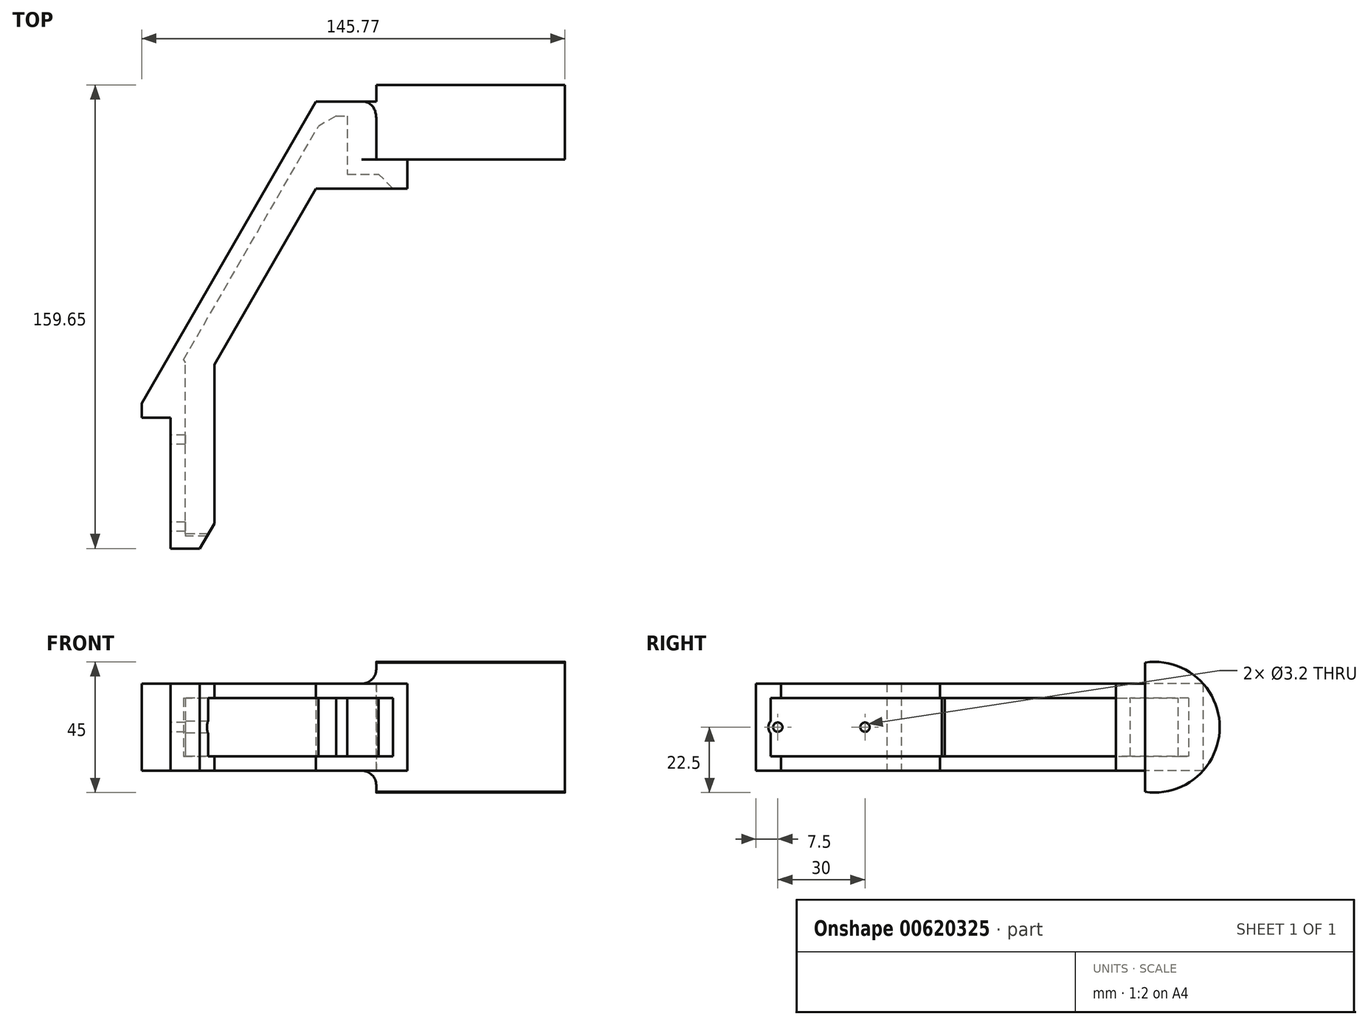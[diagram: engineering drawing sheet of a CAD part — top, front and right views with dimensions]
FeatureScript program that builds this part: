
annotation { "Feature Type Name" : "Feature", "Feature Type Description" : "" }
export const myFeature = defineFeature(function(context is Context, id is Id, definition is map)
    precondition{}
    {
        {
            var Q0;
            Q0=qCreatedBy(makeId("Top.planeOp"),FACE);
            var sketch = newSketch(context, id + "F0", { "sketchPlane" : qUnion([Q0])});
            skLineSegment(sketch, "E0", {"start": v(-10, 0) * mm, "end": v(-10, 5) * mm});
            skLineSegment(sketch, "E1", {"start": v(-10, 5) * mm, "end": v(50, 108.92) * mm});
            skLineSegment(sketch, "E2", {"start": v(81.55, 78.92) * mm, "end": v(10, -45) * mm});
            skLineSegment(sketch, "E3", {"start": v(10, -45) * mm, "end": v(0, -45) * mm});
            skLineSegment(sketch, "E4", {"start": v(50, 108.92) * mm, "end": v(65.77, 108.92) * mm});
            skLineSegment(sketch, "E5", {"start": v(81.55, 88.92) * mm, "end": v(81.55, 78.92) * mm});
            skLineSegment(sketch, "E6", {"start": v(0, -45) * mm, "end": v(0, 0) * mm});
            skLineSegment(sketch, "E7", {"start": v(0, 0) * mm, "end": v(-10, 0) * mm});
            skPoint(sketch, "E8.orphan", {"position": v(-10, -45) * mm});
            skLineSegment(sketch, "E9", {"start": v(65.77, 108.92) * mm, "end": v(65.77, 88.92) * mm});
            skLineSegment(sketch, "E10", {"start": v(65.77, 88.92) * mm, "end": v(81.55, 88.92) * mm});
            skPoint(sketch, "E11.orphan", {"position": v(81.55, 108.92) * mm});
            skSolve(sketch);
        }
        {
            var Q0;
            Q0=makeQuery(id+"F0.imprint","IMPRINT",FACE,{"disambiguationData":[TD([[makeQuery(id+"F0.imprint","IMPRINT",EDGE,{"derivedFrom":sQuery(id+"F0.wireOp",EDGE,"E0")}),-1.0]])]});
            extrude(context, id + "F1", {"entities" : qUnion([Q0]), "depth" : 30 * mm, "offsetDistance" : 25 * mm});
        }
        {
            var Q0;
            Q0=makeQuery(id+"F1.opExtrude","SWEPT_FACE",FACE,{"disambiguationData":[OSD([sQuery(id+"F0.wireOp",EDGE,"E2")])]});
            shell(context, id + "F2", {"entities" : qUnion([Q0]), "thickness" : 5 * mm});
        }
        {
            var Q0;
            Q0=makeQuery(id+"F1.opExtrude","SWEPT_FACE",FACE,{"disambiguationData":[OSD([sQuery(id+"F0.wireOp",EDGE,"E6")])]});
            var sketch = newSketch(context, id + "F3", { "sketchPlane" : qUnion([Q0])});
            skCircle(sketch, "E12", {"center": v(7.5, 15) * mm, "radius": 1.6 * mm});
            skCircle(sketch, "E13", {"center": v(37.5, 15) * mm, "radius": 1.6 * mm});
            skLineSegment(sketch, "E14", {"start": v(45, 15) * mm, "end": v(0, 15) * mm, "construction": true});
            skLineSegment(sketch, "E15", {"start": v(22.5, 30) * mm, "end": v(22.5, 0) * mm, "construction": true});
            skSolve(sketch);
        }
        {
            var Q0;
            Q0=makeQuery(id+"F3.imprint","IMPRINT",FACE,{"disambiguationData":[TD([[makeQuery(id+"F3.imprint","IMPRINT",EDGE,{"derivedFrom":sQuery(id+"F3.wireOp",EDGE,"E12")}),1.0]])]});
            var Q1;
            Q1=makeQuery(id+"F3.imprint","IMPRINT",FACE,{"disambiguationData":[TD([[makeQuery(id+"F3.imprint","IMPRINT",EDGE,{"derivedFrom":sQuery(id+"F3.wireOp",EDGE,"E13")}),1.0]])]});
            extrude(context, id + "F4", {"entities" : qUnion([Q0, Q1]), "operationType" : NewBodyOperationType.REMOVE, "endBound" : BoundingType.THROUGH_ALL, "oppositeDirection" : true, "depth" : 25 * mm, "offsetDistance" : 25 * mm});
        }
        {
            var Q0;
            Q0=makeQuery(id+"F1.opExtrude","CAP_FACE",FACE,{"disambiguationData":[OSD([sQuery(id+"F0.wireOp",EDGE,"E0"),sQuery(id+"F0.wireOp",EDGE,"E1"),sQuery(id+"F0.wireOp",EDGE,"E2"),sQuery(id+"F0.wireOp",EDGE,"E3"),sQuery(id+"F0.wireOp",EDGE,"E4"),sQuery(id+"F0.wireOp",EDGE,"E5"),sQuery(id+"F0.wireOp",EDGE,"E6"),sQuery(id+"F0.wireOp",EDGE,"E7"),sQuery(id+"F0.wireOp",EDGE,"E9"),sQuery(id+"F0.wireOp",EDGE,"E10")])],"isStart":false});
            var sketch = newSketch(context, id + "F5", { "sketchPlane" : qUnion([Q0])});
            skLineSegment(sketch, "E16", {"start": v(15, -36.34) * mm, "end": v(15, 18.3) * mm});
            skLineSegment(sketch, "E17", {"start": v(15, 18.3) * mm, "end": v(50, 78.92) * mm});
            skLineSegment(sketch, "E18", {"start": v(50, 78.92) * mm, "end": v(81.55, 78.92) * mm});
            skSolve(sketch);
        }
        {
            var Q0;
            {var subQ0=sQuery(id+"F5.wireOp",EDGE,"E16");Q0=makeQuery(id+"F5.imprint","IMPRINT",FACE,{"disambiguationData":[TD([[makeQuery(id+"F5.imprint","IMPRINT",EDGE,{"derivedFrom":subQ0}),-1.0]])]});}
            extrude(context, id + "F6", {"entities" : qUnion([Q0]), "operationType" : NewBodyOperationType.REMOVE, "endBound" : BoundingType.THROUGH_ALL, "oppositeDirection" : true, "depth" : 25 * mm, "offsetDistance" : 25 * mm});
        }
        {
            var Q0;
            {var subQ0=sQuery(id+"F0.wireOp",EDGE,"E10");Q0=makeQuery(id+"FjHifU373DTVq5l_1.boolean.opBoolean","MERGE",FACE,{"derivedFrom":[makeQuery(id+"F1.opExtrude","SWEPT_FACE",FACE,{"disambiguationData":[OSD([subQ0])]}),makeQuery(id+"FjHifU373DTVq5l_1.opExtrude","CAP_FACE",FACE,{"disambiguationData":[OSD([subQ0])],"isStart":false})]});}
            var sketch = newSketch(context, id + "F7", { "sketchPlane" : qUnion([Q0])});
            skLineSegment(sketch, "E19", {"start": v(-65.77, 30) * mm, "end": v(-135.77, 30) * mm});
            skLineSegment(sketch, "E20", {"start": v(-135.77, 30) * mm, "end": v(-135.77, 0) * mm});
            skLineSegment(sketch, "E21", {"start": v(-135.77, 0) * mm, "end": v(-65.77, 0) * mm});
            skSolve(sketch);
        }
        {
            var Q0;
            {var subQ2=sQuery(id+"F7.wireOp",EDGE,"E20");Q0=makeQuery(id+"F7.imprint","IMPRINT",FACE,{"disambiguationData":[TD([[makeQuery(id+"F7.imprint","IMPRINT",EDGE,{"derivedFrom":subQ2}),1.0]])]});}
            var Q1;
            {var subQ7=sQuery(id+"F7.wireOp",EDGE,"d07ecf7d-7c7d-4d48-b3f6-4453b43f33c9.0");Q1=makeQuery(id+"F7.imprint","IMPRINT",FACE,{"disambiguationData":[TD([[makeQuery(id+"F7.imprint","IMPRINT",EDGE,{"derivedFrom":subQ7}),-1.0]])]});}
            var Q2;
            {var subQ7=sQuery(id+"F7.wireOp",EDGE,"e0d4764e-986f-4d8b-bff7-2879278c111d.0.2");Q2=makeQuery(id+"F7.imprint","IMPRINT",FACE,{"disambiguationData":[TD([[makeQuery(id+"F7.imprint","IMPRINT",EDGE,{"derivedFrom":subQ7}),-1.0]])]});}
            var Q3;
            {var subQ1=sQuery(id+"F0.wireOp",EDGE,"E10");var subQ2=makeQuery(id+"F1.opExtrude","SWEPT_EDGE",EDGE,{"disambiguationData":[OSD([sQuery(id+"F0.wireOp",EDGE,"E5"),subQ1])]});Q3=makeQuery(id+"F7.imprint","IMPRINT",FACE,{"disambiguationData":[TD([[makeQuery(id+"F7.imprint","IMPRINT",EDGE,{"derivedFrom":subQ2}),1.0]])]});}
            extrude(context, id + "F8", {"entities" : qUnion([Q0, Q1, Q2, Q3]), "depth" : 20 * mm, "offsetDistance" : 25 * mm});
        }
        {
            var Q0;
            Q0=makeQuery(id+"F8.opExtrude","SWEPT_FACE",FACE,{"disambiguationData":[OSD([sQuery(id+"F7.wireOp",EDGE,"E20")])]});
            var sketch = newSketch(context, id + "F9", { "sketchPlane" : qUnion([Q0])});
            skArc(sketch, "E22", {"start": v(88.92, -7.27) * mm, "mid": v(114.65, 15) * mm, "end": v(88.92, 37.27) * mm});
            skLineSegment(sketch, "E23", {"start": v(88.92, 30) * mm, "end": v(88.92, 37.27) * mm});
            skLineSegment(sketch, "E24", {"start": v(88.92, 0) * mm, "end": v(88.92, -7.27) * mm});
            skSolve(sketch);
        }
        {
            var Q0;
            {var subQ1=sQuery(id+"F7.wireOp",EDGE,"E20");var subQ2=makeQuery(id+"F8.opExtrude","CAP_EDGE",EDGE,{"disambiguationData":[OSD([subQ1])],"isStart":false});Q0=makeQuery(id+"F9.imprint","IMPRINT",FACE,{"disambiguationData":[TD([[makeQuery(id+"F9.imprint","IMPRINT",EDGE,{"derivedFrom":subQ2}),1.0]])]});}
            var Q1;
            {var subQ3=sQuery(id+"F9.wireOp",EDGE,"E23");Q1=makeQuery(id+"F9.imprint","IMPRINT",FACE,{"disambiguationData":[TD([[makeQuery(id+"F9.imprint","IMPRINT",EDGE,{"derivedFrom":subQ3}),-1.0]])]});}
            var Q2;
            {var subQ3=sQuery(id+"F9.wireOp",EDGE,"E24");Q2=makeQuery(id+"F9.imprint","IMPRINT",FACE,{"disambiguationData":[TD([[makeQuery(id+"F9.imprint","IMPRINT",EDGE,{"derivedFrom":subQ3}),1.0]])]});}
            extrude(context, id + "F10", {"entities" : qUnion([Q0, Q1, Q2]), "operationType" : NewBodyOperationType.ADD, "oppositeDirection" : true, "depth" : 65 * mm, "offsetDistance" : 25 * mm});
        }
        {
            var Q0;
            Q0=makeQuery(id+"F10.opExtrude","CAP_EDGE",EDGE,{"disambiguationData":[OSD([sQuery(id+"F7.wireOp",EDGE,"E19"),sQuery(id+"F7.wireOp",EDGE,"E20")])],"isStart":false});
            var Q1;
            Q1=makeQuery(id+"F10.opExtrude","CAP_EDGE",EDGE,{"disambiguationData":[OSD([sQuery(id+"F7.wireOp",EDGE,"E20"),sQuery(id+"F7.wireOp",EDGE,"E21")])],"isStart":false});
            fillet(context, id + "F11", {"entities" : qUnion([Q0, Q1]), "radius" : 5 * mm, "tangentPropagation" : true, "allowEdgeOverflow" : false});
        }
        {
            var Q0;
            Q0=makeQuery(id+"F2.opShell","TWEAK_EDGE",EDGE,{"derivedFrom":[makeQuery(id+"F1.opExtrude","SWEPT_FACE",FACE,{"disambiguationData":[OSD([sQuery(id+"F0.wireOp",EDGE,"E1")])]}),makeQuery(id+"F1.opExtrude","SWEPT_FACE",FACE,{"disambiguationData":[OSD([sQuery(id+"F0.wireOp",EDGE,"E7")])]})]});
            chamfer(context, id + "F12", {"entities" : qUnion([Q0]), "width" : 10 * mm, "tangentPropagation" : true});
        }
        {
            var Q0;
            Q0=makeQuery(id+"F2.opShell","OFFSET_FACE",FACE,{"disambiguationData":[OSD([sQuery(id+"F0.wireOp",EDGE,"E6")])]});
            var sketch = newSketch(context, id + "F13", { "sketchPlane" : qUnion([Q0])});
            skCircle(sketch, "E25", {"center": v(-37.5, 15) * mm, "radius": 3.25 * mm});
            skSolve(sketch);
        }
        {
            var Q0;
            {var subQ0=sQuery(id+"F13.wireOp",EDGE,"E25");var subQ1=makeQuery(id+"F2.opShell","OFFSET_EDGE",EDGE,{"disambiguationData":[OSD([sQuery(id+"F0.wireOp",EDGE,"E3"),sQuery(id+"F0.wireOp",EDGE,"E6")])]});var subQ2=makeQuery(id+"F13.imprint","INTERSECT",VERTEX,{"disambiguationData":[OD(0.0)],"derivedFrom":[subQ1,subQ0]});Q0=makeQuery(id+"F13.imprint","IMPRINT",FACE,{"disambiguationData":[TD([[makeQuery(id+"F13.imprint","IMPRINT",EDGE,{"disambiguationData":[TD([[subQ2,1.0]])],"derivedFrom":subQ0}),1.0]])]});}
            extrude(context, id + "F14", {"entities" : qUnion([Q0]), "operationType" : NewBodyOperationType.REMOVE, "depth" : 25 * mm, "offsetDistance" : 25 * mm});
        }
        {
            var Q0;
            Q0=makeQuery(id+"F2.opShell","OFFSET_EDGE",EDGE,{"disambiguationData":[OSD([sQuery(id+"F0.wireOp",EDGE,"E1"),sQuery(id+"F0.wireOp",EDGE,"E4")])]});
            chamfer(context, id + "F15", {"entities" : qUnion([Q0]), "width" : 7 * mm, "tangentPropagation" : true});
        }
        {
            var Q0;
            Q0=makeQuery(id+"F2.opShell","OFFSET_EDGE",EDGE,{"disambiguationData":[OSD([sQuery(id+"F0.wireOp",EDGE,"E5"),sQuery(id+"F0.wireOp",EDGE,"E10")])]});
            chamfer(context, id + "F16", {"entities" : qUnion([Q0]), "width" : 5 * mm, "tangentPropagation" : true});
        }
    });
